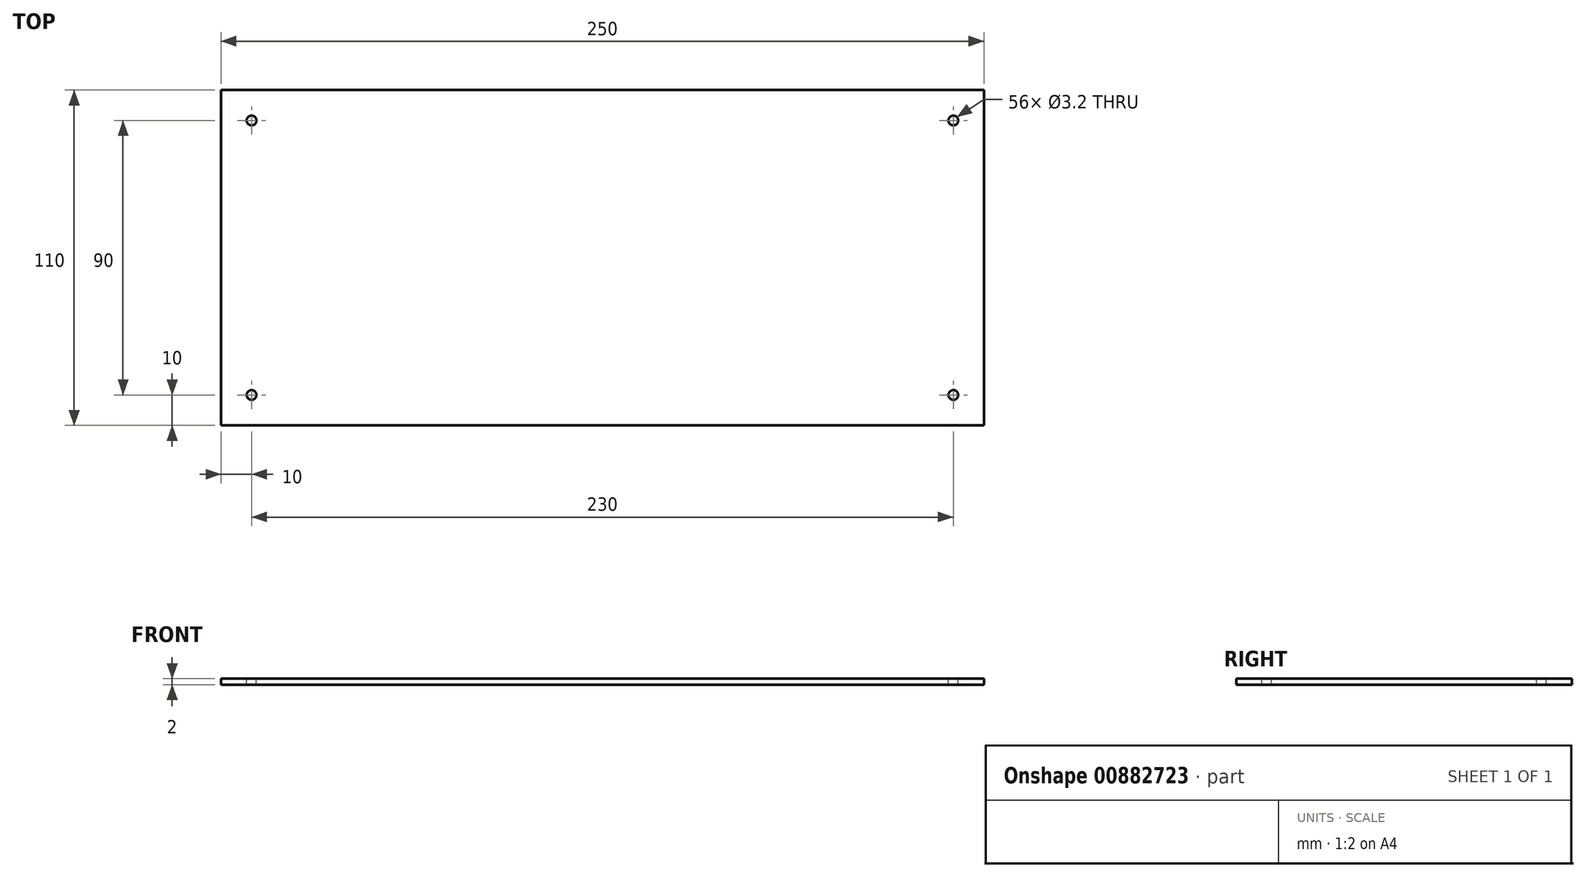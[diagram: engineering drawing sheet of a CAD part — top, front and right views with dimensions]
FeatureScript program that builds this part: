
annotation { "Feature Type Name" : "Feature", "Feature Type Description" : "" }
export const myFeature = defineFeature(function(context is Context, id is Id, definition is map)
    precondition{}
    {
        {
            var Q0;
            Q0=qCreatedBy(makeId("Top.planeOp"),FACE);
            var sketch = newSketch(context, id + "F0", { "sketchPlane" : qUnion([Q0])});
            skLineSegment(sketch, "E0.bottom", {"start": v(125, 55) * mm, "end": v(-125, 55) * mm});
            skLineSegment(sketch, "E0.top", {"start": v(125, -55) * mm, "end": v(-125, -55) * mm});
            skLineSegment(sketch, "E0.left", {"start": v(125, 55) * mm, "end": v(125, -55) * mm});
            skLineSegment(sketch, "E0.right", {"start": v(-125, 55) * mm, "end": v(-125, -55) * mm});
            skPoint(sketch, "E0.middle", {"position": v(0, 0) * mm});
            skSolve(sketch);
        }
        {
            var Q0;
            Q0=makeQuery(id+"F0.imprint","IMPRINT",FACE,{"disambiguationData":[TD([[makeQuery(id+"F0.imprint","IMPRINT",EDGE,{"derivedFrom":sQuery(id+"F0.wireOp",EDGE,"E0.bottom")}),1.0]])]});
            extrude(context, id + "F1", {"entities" : qUnion([Q0]), "depth" : 2 * mm, "offsetDistance" : 25 * mm});
        }
        {
            var Q0;
            Q0=makeQuery(id+"F1.opExtrude","CAP_FACE",FACE,{"disambiguationData":[OSD([sQuery(id+"F0.wireOp",EDGE,"E0.bottom"),sQuery(id+"F0.wireOp",EDGE,"E0.top"),sQuery(id+"F0.wireOp",EDGE,"E0.left"),sQuery(id+"F0.wireOp",EDGE,"E0.right")])],"isStart":false});
            var sketch = newSketch(context, id + "F2", { "sketchPlane" : qUnion([Q0])});
            skPoint(sketch, "E1", {"position": v(-115, -45) * mm});
            skPoint(sketch, "E2.MirrorP", {"position": v(115, -45) * mm});
            skPoint(sketch, "E3.MirrorP", {"position": v(-115, 45) * mm});
            skPoint(sketch, "E4.MirrorP", {"position": v(115, 45) * mm});
            skSolve(sketch);
        }
        {
            var Q0;
            Q0=sQuery(id+"F2.wireOp",VERTEX,"E3.MirrorP");
            var Q1;
            Q1=sQuery(id+"F2.wireOp",VERTEX,"E1");
            var Q2;
            Q2=sQuery(id+"F2.wireOp",VERTEX,"E2.MirrorP");
            var Q3;
            Q3=sQuery(id+"F2.wireOp",VERTEX,"E4.MirrorP");
            var Q4;
            Q4=makeQuery(id+"F1.opExtrude","SWEPT_BODY",BODY,{"disambiguationData":[OSD([sQuery(id+"F0.wireOp",EDGE,"E0.bottom"),sQuery(id+"F0.wireOp",EDGE,"E0.top"),sQuery(id+"F0.wireOp",EDGE,"E0.left"),sQuery(id+"F0.wireOp",EDGE,"E0.right")])]});
            hole(context, id + "F3", {"style" : HoleStyle.SIMPLE, "endStyle" : HoleEndStyle.BLIND, "holeDiameter" : 3.2 * mm, "majorDiameter" : 5 * mm, "holeDepth" : 7 * mm, "isTappedThrough" : true, "tappedDepth" : 12 * mm, "tapClearance" : 3, "locations" : qUnion([Q0, Q1, Q2, Q3]), "scope" : qUnion([Q4])});
        }
    });
